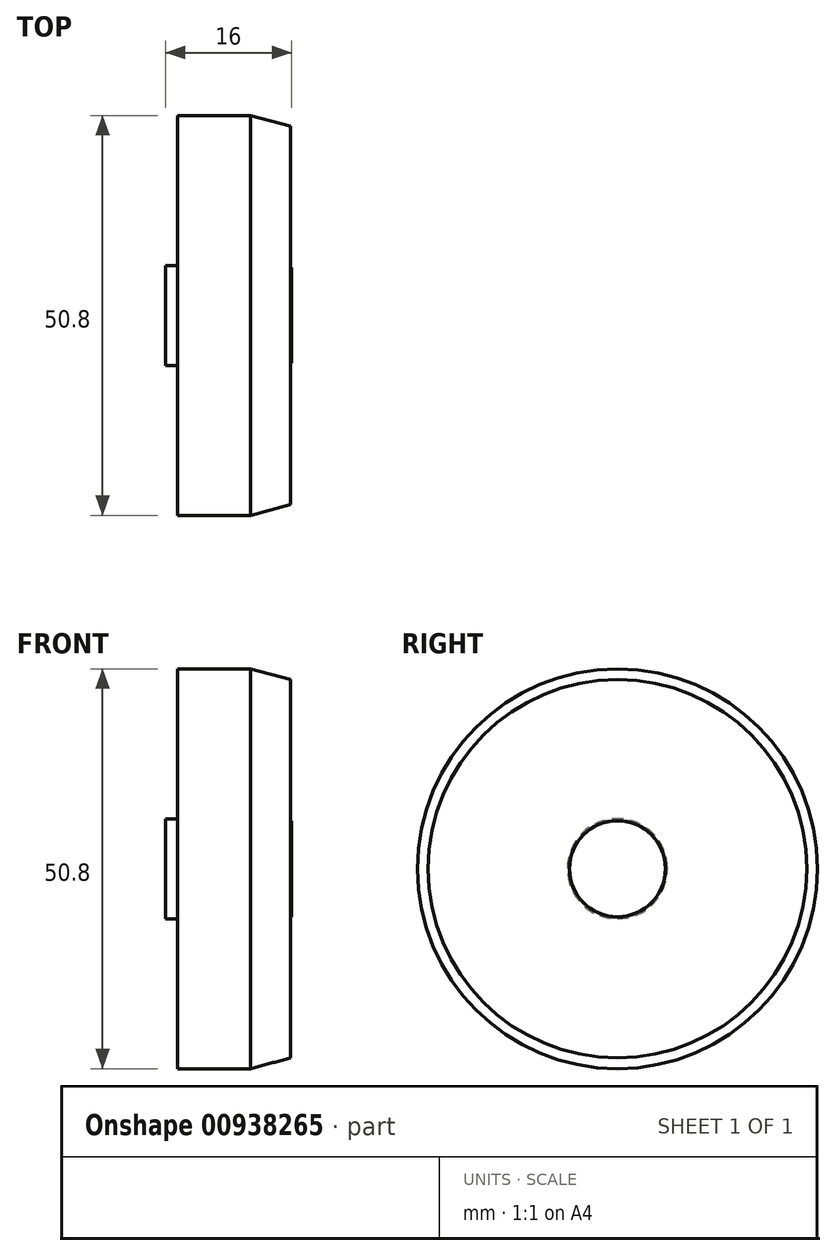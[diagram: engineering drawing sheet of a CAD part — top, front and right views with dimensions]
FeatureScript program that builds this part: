
annotation { "Feature Type Name" : "Feature", "Feature Type Description" : "" }
export const myFeature = defineFeature(function(context is Context, id is Id, definition is map)
    precondition{}
    {
        {
            var Q0;
            Q0=qCreatedBy(makeId("Right.planeOp"),FACE);
            var sketch = newSketch(context, id + "F0", { "sketchPlane" : qUnion([Q0])});
            skCircle(sketch, "E0", {"center": v(0, 0) * mm, "radius": 25.4 * mm});
            skSolve(sketch);
        }
        {
            var Q0;
            Q0=qSketchRegion(id+"F0",true);
            extrude(context, id + "F1", {"entities" : qUnion([Q0]), "depth" : 9.65 * mm, "offsetDistance" : 25.4 * mm});
        }
        {
            var Q0;
            Q0=makeQuery(id+"F1.opExtrude","CAP_FACE",FACE,{"disambiguationData":[OSD([sQuery(id+"F0.wireOp",EDGE,"E0")])],"isStart":false});
            var sketch = newSketch(context, id + "F2", { "sketchPlane" : qUnion([Q0])});
            skCircle(sketch, "E1", {"center": v(0, 0) * mm, "radius": 4.76 * mm});
            skSolve(sketch);
        }
        {
            var Q0;
            Q0=qSketchRegion(id+"F2",true);
            extrude(context, id + "F3", {"entities" : qUnion([Q0]), "operationType" : NewBodyOperationType.ADD, "depth" : 4.83 * mm, "offsetDistance" : 25.4 * mm});
        }
        {
            var Q0;
            Q0=makeQuery(id+"F1.opExtrude","CAP_FACE",FACE,{"disambiguationData":[OSD([sQuery(id+"F0.wireOp",EDGE,"E0")])],"isStart":false});
            extrude(context, id + "F4", {"entities" : qUnion([Q0]), "operationType" : NewBodyOperationType.ADD, "depth" : 4.7 * mm, "offsetDistance" : 25.4 * mm});
        }
        {
            var Q0;
            Q0=makeQuery(id+"F4.opExtrude","CAP_FACE",FACE,{"disambiguationData":[OSD([sQuery(id+"F0.wireOp",EDGE,"E0")])],"isStart":false});
            chamfer(context, id + "F5", {"entities" : qUnion([Q0]), "chamferType" : ChamferType.OFFSET_ANGLE, "width" : 5.08 * mm, "oppositeDirection" : false, "angle" : 15 * degree});
        }
        {
            var Q0;
            Q0=makeQuery(id+"F1.opExtrude","CAP_FACE",FACE,{"disambiguationData":[OSD([sQuery(id+"F0.wireOp",EDGE,"E0")])],"isStart":true});
            extrude(context, id + "F6", {"entities" : qUnion([Q0]), "operationType" : NewBodyOperationType.REMOVE, "depth" : 3.17 * mm, "offsetDistance" : 25.4 * mm});
        }
        {
            var Q0;
            Q0=makeQuery(id+"F1.opExtrude","CAP_FACE",FACE,{"disambiguationData":[OSD([sQuery(id+"F0.wireOp",EDGE,"E0")])],"isStart":true});
            var sketch = newSketch(context, id + "F7", { "sketchPlane" : qUnion([Q0])});
            skCircle(sketch, "E2", {"center": v(0, 0) * mm, "radius": 6.35 * mm});
            skSolve(sketch);
        }
        {
            var Q0;
            Q0=qSketchRegion(id+"F7",true);
            extrude(context, id + "F8", {"entities" : qUnion([Q0]), "operationType" : NewBodyOperationType.ADD, "depth" : 1.52 * mm, "offsetDistance" : 25.4 * mm});
        }
    });
